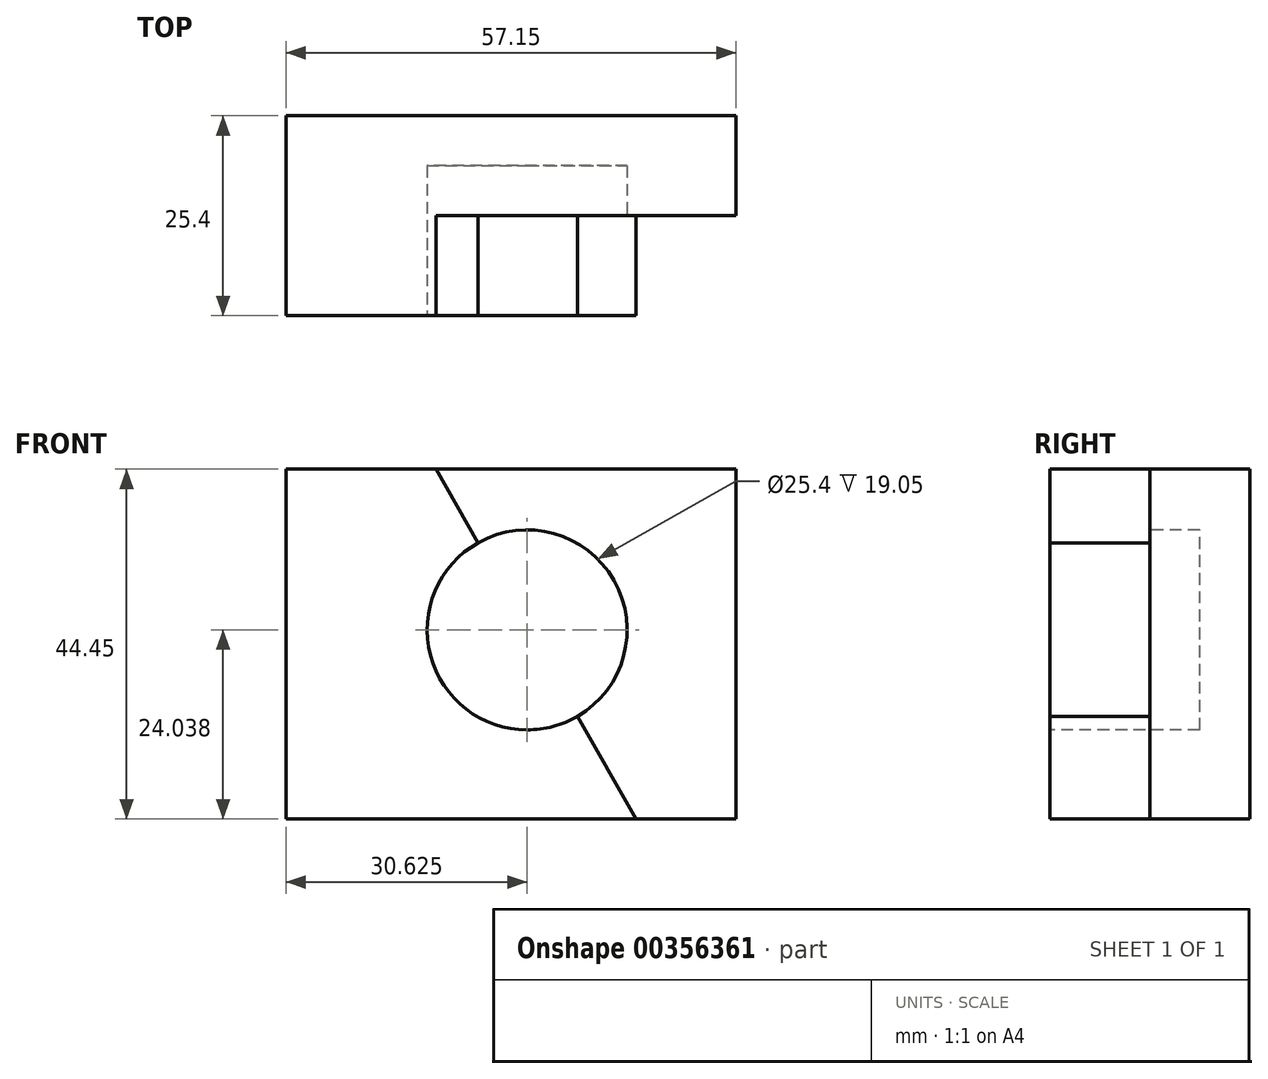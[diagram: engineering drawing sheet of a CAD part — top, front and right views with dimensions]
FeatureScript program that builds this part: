
annotation { "Feature Type Name" : "Feature", "Feature Type Description" : "" }
export const myFeature = defineFeature(function(context is Context, id is Id, definition is map)
    precondition{}
    {
        {
            var Q0;
            Q0=qCreatedBy(makeId("Front.planeOp"),FACE);
            var sketch = newSketch(context, id + "F0", { "sketchPlane" : qUnion([Q0])});
            skLineSegment(sketch, "E0.bottom", {"start": v(0, 0) * mm, "end": v(57.15, 0) * mm});
            skLineSegment(sketch, "E0.top", {"start": v(0, 44.45) * mm, "end": v(57.15, 44.45) * mm});
            skLineSegment(sketch, "E0.left", {"start": v(0, 0) * mm, "end": v(0, 44.45) * mm});
            skLineSegment(sketch, "E0.right", {"start": v(57.15, 0) * mm, "end": v(57.15, 44.45) * mm});
            skSolve(sketch);
        }
        {
            var Q0;
            Q0 = qSketchRegion(id + "F0", true);
            extrude(context, id + "F1", {"entities" : qUnion([Q0]), "depth" : 25.4 * mm});
        }
        {
            var Q0;
            Q0=makeQuery(id+"F1.opExtrude","CAP_FACE",FACE,{"disambiguationData":[OSD([sQuery(id+"F0.wireOp",EDGE,"E0.bottom"),sQuery(id+"F0.wireOp",EDGE,"E0.top"),sQuery(id+"F0.wireOp",EDGE,"E0.left"),sQuery(id+"F0.wireOp",EDGE,"E0.right")])],"isStart":false});
            var sketch = newSketch(context, id + "F2", { "sketchPlane" : qUnion([Q0])});
            skLineSegment(sketch, "E1", {"start": v(19.05, 44.45) * mm, "end": v(44.45, 0) * mm});
            skArc(sketch, "E2", {"start": v(24.4, 35.1) * mm, "mid": v(19.6, 17.74) * mm, "end": v(37, 13.05) * mm});
            skArc(sketch, "E3", {"start": v(37, 13.05) * mm, "mid": v(41.65, 30.34) * mm, "end": v(24.4, 35.1) * mm});
            skSolve(sketch);
        }
        {
            var Q0;
            {var subQ6=makeQuery(id+"F1.opExtrude","CAP_EDGE",EDGE,{"disambiguationData":[OSD([sQuery(id+"F0.wireOp",EDGE,"E0.right")])],"isStart":false});Q0=makeQuery(id+"F2.imprint","IMPRINT",FACE,{"disambiguationData":[TD([[makeQuery(id+"F2.imprint","IMPRINT",EDGE,{"derivedFrom":subQ6}),1.0]])]});}
            extrude(context, id + "F3", {"entities" : qUnion([Q0]), "operationType" : NewBodyOperationType.REMOVE, "oppositeDirection" : true, "depth" : 12.7 * mm});
        }
        {
            var Q0;
            Q0 = qSketchRegion(id + "F2", true);
            extrude(context, id + "F4", {"entities" : qUnion([Q0]), "operationType" : NewBodyOperationType.REMOVE, "oppositeDirection" : true, "depth" : 19.05 * mm});
        }
    });
